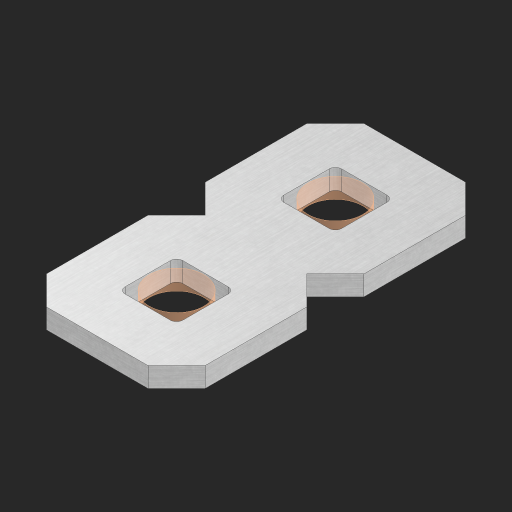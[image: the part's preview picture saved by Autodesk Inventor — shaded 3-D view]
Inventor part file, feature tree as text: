
AUTODESK INVENTOR PART (.ipt)
format: ipt  version: 2023 (Build 270158000, 158)  size: 308,736 bytes
history: native  units: in
note: dims shown in document units (in); Inventor stores cm internally (conversion verified against a paired STEP export)
features: other x3, sketch x2, pattern_linear x1, extrude x1
ambient origin geometry x8: Origin, YZ Plane, XZ Plane, XY Plane, X Axis, Y Axis, Z Axis, Center Point
bodies: Solid1 (feature_tree), Body (feature_tree)
feature tree (7):
  pattern_linear  "Rectangular Pattern1"  Spacing1=0.09in  [1 undecoded]
  sketch  "Sketch1"  dims[d1=0.5in]
  sketch  "Sketch2"  dims[d2=0.182in d3=0.09in d4=0.09in d5=0.09in d6=0.09in d7=0.09in d8=0.09in d9=0.09in d10=0.09in d11=0.02in d13=0.0in d14=0.172in d15=0.0625in d16=0.0in d19=0.5in d22=0.5in]
  other  "Srf1"
  other  "Srf126"
  other  "Circle"
  extrude  "ExtrusionSrf126"  Depth=0.09in
note: 1 required parameter value undecoded (feature->parameter linkage not recoverable at this tier; creation-order binding heuristic only, values carry confidence <= 0.55)
